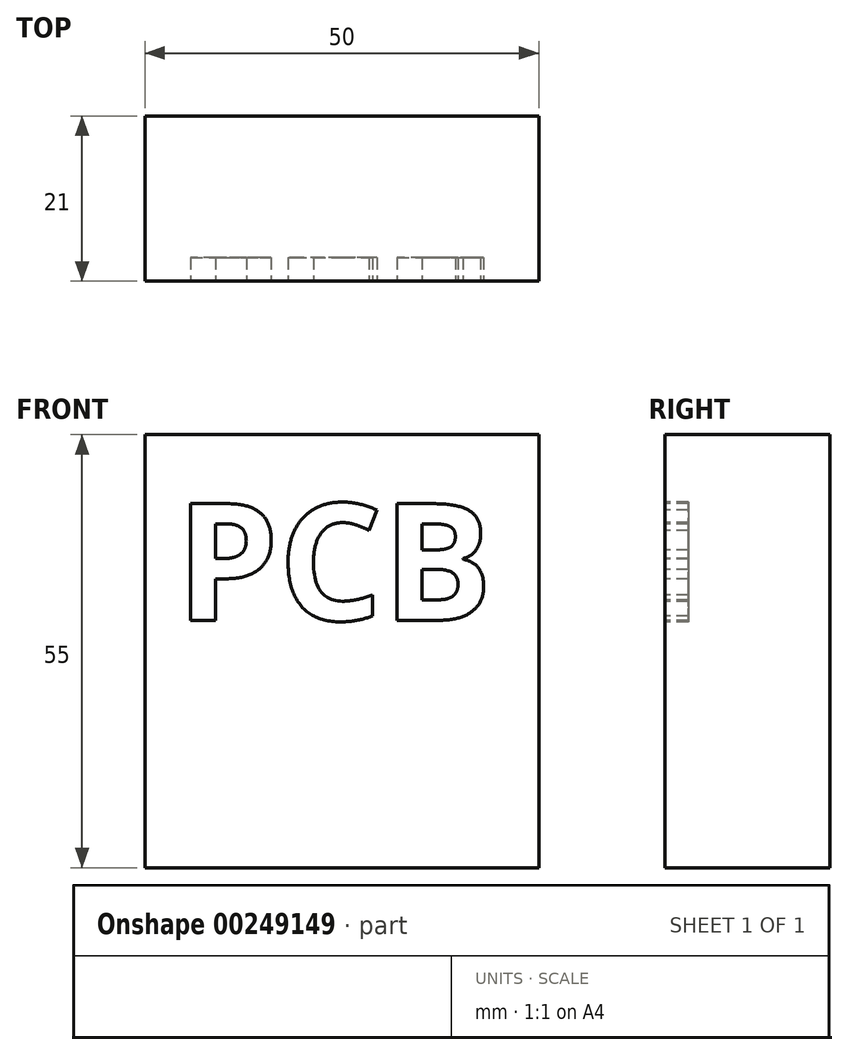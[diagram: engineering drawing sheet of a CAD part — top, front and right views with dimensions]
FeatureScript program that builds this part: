
annotation { "Feature Type Name" : "Feature", "Feature Type Description" : "" }
export const myFeature = defineFeature(function(context is Context, id is Id, definition is map)
    precondition{}
    {
        {
            var Q0;
            Q0=qCreatedBy(makeId("Front.planeOp"),FACE);
            var sketch = newSketch(context, id + "F0", { "sketchPlane" : qUnion([Q0])});
            skLineSegment(sketch, "E0.bottom", {"start": v(25, -27.5) * mm, "end": v(-25, -27.5) * mm});
            skLineSegment(sketch, "E0.top", {"start": v(25, 27.5) * mm, "end": v(-25, 27.5) * mm});
            skLineSegment(sketch, "E0.left", {"start": v(25, -27.5) * mm, "end": v(25, 27.5) * mm});
            skLineSegment(sketch, "E0.right", {"start": v(-25, -27.5) * mm, "end": v(-25, 27.5) * mm});
            skPoint(sketch, "E0.middle", {"position": v(0, 0) * mm});
            skSolve(sketch);
        }
        {
            var Q0;
            Q0 = qSketchRegion(id + "F0", true);
            extrude(context, id + "F1", {"entities" : qUnion([Q0]), "depth" : 21 * mm});
        }
        {
            var Q0;
            Q0=makeQuery(id+"F1.opExtrude","CAP_FACE",FACE,{"disambiguationData":[OSD([sQuery(id+"F0.wireOp",EDGE,"E0.bottom"),sQuery(id+"F0.wireOp",EDGE,"E0.top"),sQuery(id+"F0.wireOp",EDGE,"E0.left"),sQuery(id+"F0.wireOp",EDGE,"E0.right")])],"isStart":false});
            var sketch = newSketch(context, id + "F2", { "sketchPlane" : qUnion([Q0])});
            skSolve(sketch);
        }
        {
            var Q0;
            Q0=makeQuery(id+"F2.imprint","IMPRINT",FACE,{"disambiguationData":[TD([[makeQuery(id+"F2.imprint","IMPRINT",EDGE,{"derivedFrom":makeQuery(id+"F1.opExtrude","CAP_EDGE",EDGE,{"disambiguationData":[OSD([sQuery(id+"F0.wireOp",EDGE,"E0.bottom")])],"isStart":false})}),-1.0]])]});
            var sketch = newSketch(context, id + "F3", { "sketchPlane" : qUnion([Q0])});
            skText(sketch, "E1", { "text": "PCB", "fontName": "OpenSans-Bold.ttf"});
            const initialGuessF3  = {"E1": [-0.02107, 0.00393, 1, 0, 0.01493]};
            skSetInitialGuess(sketch, initialGuessF3);
            skSolve(sketch);
        }
        {
            var Q0;
            Q0 = qSketchRegion(id + "F3", true);
            extrude(context, id + "F4", {"entities" : qUnion([Q0]), "operationType" : NewBodyOperationType.REMOVE, "oppositeDirection" : true, "depth" : 3 * mm});
        }
    });
